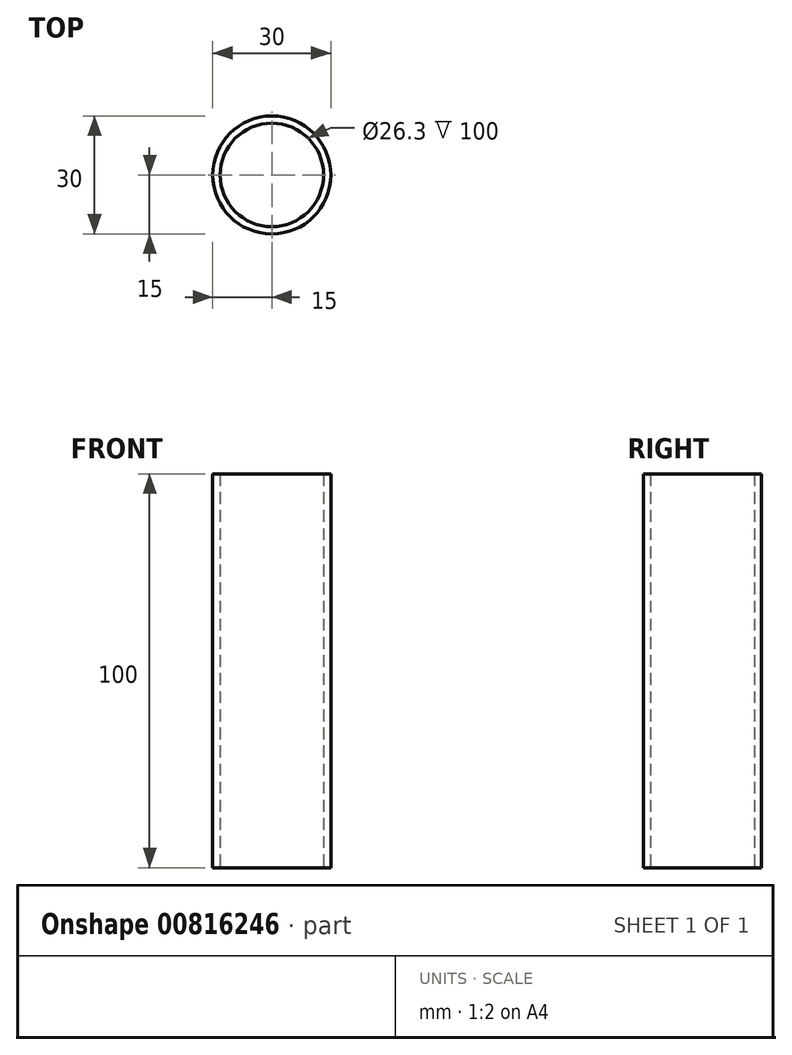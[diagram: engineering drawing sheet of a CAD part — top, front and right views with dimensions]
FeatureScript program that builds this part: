
annotation { "Feature Type Name" : "Feature", "Feature Type Description" : "" }
export const myFeature = defineFeature(function(context is Context, id is Id, definition is map)
    precondition{}
    {
        {
            var Q0;
            Q0=qCreatedBy(makeId("Top.planeOp"),FACE);
            var sketch = newSketch(context, id + "F0", { "sketchPlane" : qUnion([Q0])});
            skCircle(sketch, "E0", {"center": v(0, 0) * mm, "radius": 15 * mm});
            skCircle(sketch, "E1", {"center": v(0, 0) * mm, "radius": 13.15 * mm});
            skSolve(sketch);
        }
        {
            var Q0;
            Q0=makeQuery(id+"F0.imprint","IMPRINT",FACE,{"disambiguationData":[TD([[makeQuery(id+"F0.imprint","IMPRINT",EDGE,{"derivedFrom":sQuery(id+"F0.wireOp",EDGE,"E0")}),1.0]])]});
            extrude(context, id + "F1", {"entities" : qUnion([Q0]), "depth" : 100 * mm, "offsetDistance" : 25 * mm});
        }
    });
